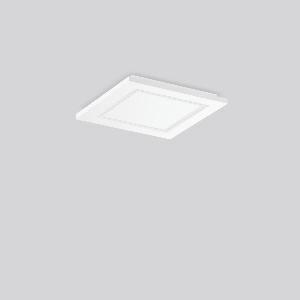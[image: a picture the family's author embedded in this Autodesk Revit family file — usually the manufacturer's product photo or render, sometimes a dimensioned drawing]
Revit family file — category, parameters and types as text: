
# Revit family: hemis_square_312188_002_2_7d0f
name_source: partatom
category: Lighting Fixtures
units: mm (PartAtom-declared; Revit-internal decimal feet)

## family parameters
Cut with Voids When Loaded = No
Host = Face
Light Source = No
Part Type = Normal
Room Calculation Point = No
Round Connector Dimension = Use Diameter
Shared = No

## types (1)
- MultiLumen 1 (1 x LED Modul 830, 2200 lm, 3000)
    Apparent Load = 16 VA
    CIE Flux Codes = 87 99 100 100 100
    Color Rendering = 80
    Color Temperature = 3000
    Default Elevation = 1800 mm
    Description = Series: HEMIS square
Glare-free LED ceiling luminaire with optical lens system. Base: metal, powder-coated, with bayonet fixing. Housing: plastic (polycarbonate). Housing and diffuser are screwed together. Diffuser with optic lenses. Big terminal block; ideal for through-wiring. Sealing strip on the back of the luminaire connects seamlessly with the ceiling. Easy installation with Plug+Play plug connection. Thanks to RUG < 22 ideal for corridors, stairways, shops, schools, meeting rooms, rest areas. 
Colour: white
Length: 300 mm
Width: 300 mm
Height: 33 mm
Lamp: LED
Socket: without socket
Colour temperature: 3000K
Colour rendering index (CRI): 80
System power: 16 W
Rated luminous flux: 2200 lm
Luminous efficiency: 138 lm/W
System power 2: 10 W
Rated luminous flux 2: 1400 lm
Luminous efficiency 2: 140 lm/W
Control gear: Regulated power supply
Protection class: I
Type of protection: IP 40
    Height = 33 mm
    Lamp = 1 x LED Modul 830
    Lamp Light Flux = 2200 lm
    Lamp count = 1
    Length = 300 mm
    Lifetime = 50000 h
    Luminous efficacy = 138 lm/W
    Manufacturer = RZB
    ModVariant = No
    Model = 312188.002.2
    Mounting Place = Ceiling
    Mounting Type = Surface mounted
    Number of Poles = 1
    OnlyDefault = Yes
    Power Factor = 1
    Product Name = HEMIS square
    Product group = Surface mounted modular luminaires
    ProductGroupID = 306
    Protection Class = Protection class I
    Protection Degree = Degree of protection
    RLX_Detail_Level = 1
    RLX_Emergency_Light_Flux = 0 lm
    RLX_Emergency_Type = 0
    RLX_Emergency_Type_DB = No
    RlxData = <blob elided: 13053 chars, md5=7a2566b3>
    Socket = socket
    Standby Power = 0 W
    System Light Flux = 2200 lm
    System Power = 16 W
    Type Comments = MultiLumen 1
    Type Image = 312188.002.jpg
    URL = http://relux.com
    VarID = multilumen_1
    Voltage = 0 V
    Weight = 0.00 kg
    Width = 300 mm

## geometry (parser evidence)
native form markers: Sweep x9
no freeform markers — native parametric forms only
